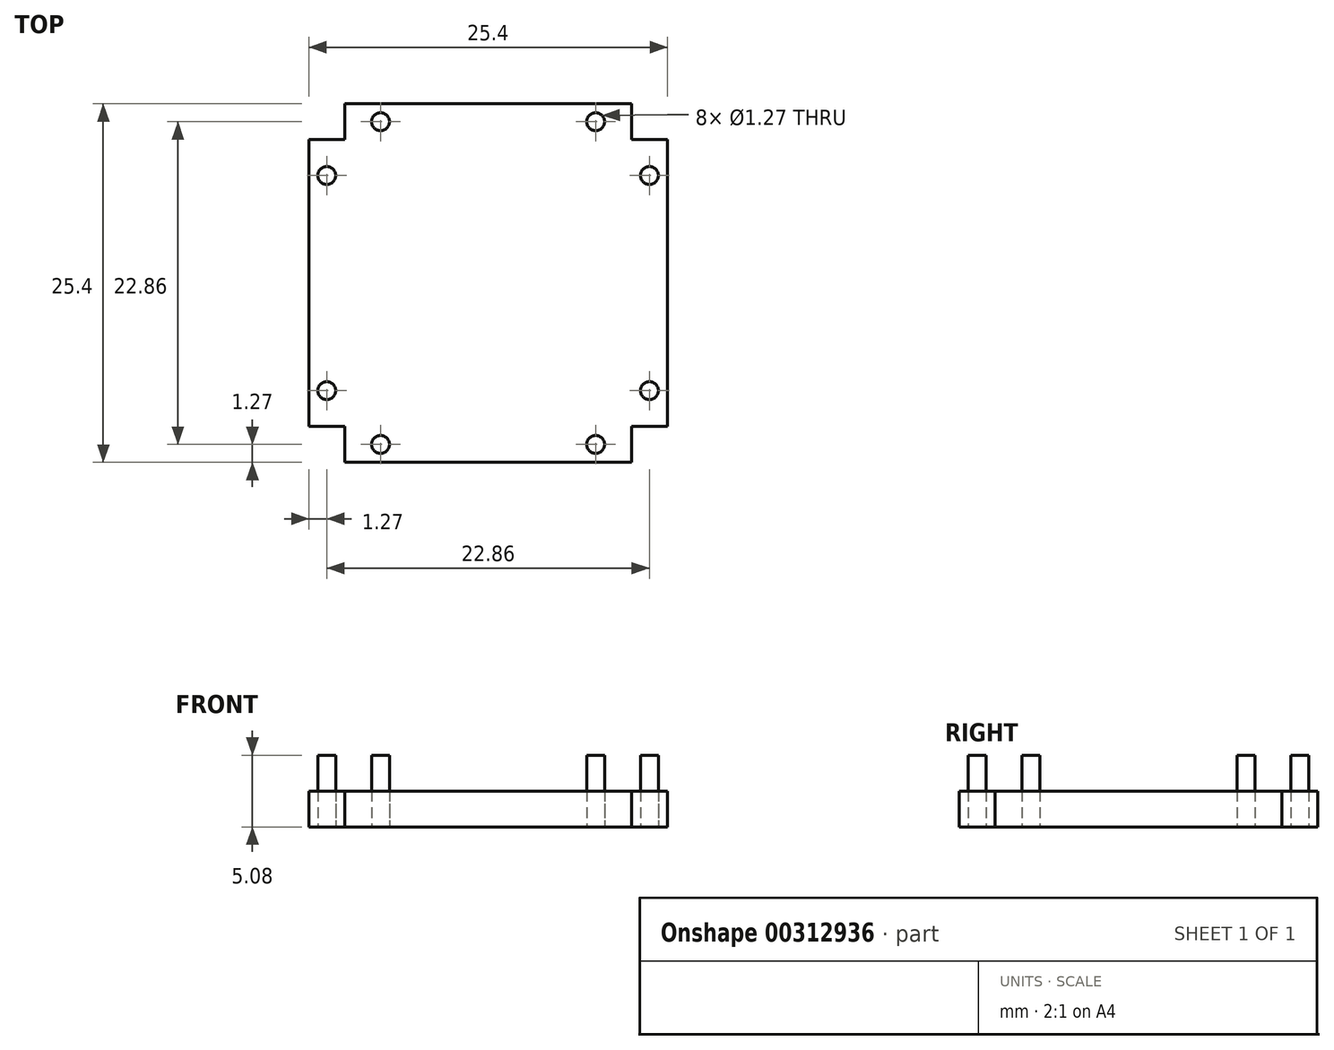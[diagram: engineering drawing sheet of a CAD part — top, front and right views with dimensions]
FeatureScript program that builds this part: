
annotation { "Feature Type Name" : "Feature", "Feature Type Description" : "" }
export const myFeature = defineFeature(function(context is Context, id is Id, definition is map)
    precondition{}
    {
        {
            var Q0;
            Q0=qCreatedBy(makeId("Top.planeOp"),FACE);
            var sketch = newSketch(context, id + "F0", { "sketchPlane" : qUnion([Q0])});
            skPoint(sketch, "E0.middle", {"position": v(0, 0) * mm});
            skLineSegment(sketch, "E1.bottom", {"start": v(10.16, -10.16) * mm, "end": v(-10.16, -10.16) * mm});
            skLineSegment(sketch, "E1.top", {"start": v(10.16, 10.16) * mm, "end": v(-10.16, 10.16) * mm});
            skLineSegment(sketch, "E1.left", {"start": v(10.16, -10.16) * mm, "end": v(10.16, 10.16) * mm});
            skLineSegment(sketch, "E1.right", {"start": v(-10.16, -10.16) * mm, "end": v(-10.16, 10.16) * mm});
            skLineSegment(sketch, "E2.bottom", {"start": v(-10.16, 10.16) * mm, "end": v(-12.7, 10.16) * mm});
            skLineSegment(sketch, "E2.left", {"start": v(-10.16, 10.16) * mm, "end": v(-10.16, 12.7) * mm});
            skLineSegment(sketch, "E3.bottom", {"start": v(10.16, 10.16) * mm, "end": v(12.7, 10.16) * mm});
            skLineSegment(sketch, "E3.left", {"start": v(10.16, 10.16) * mm, "end": v(10.16, 12.7) * mm});
            skLineSegment(sketch, "E4.bottom", {"start": v(10.16, -10.16) * mm, "end": v(12.7, -10.16) * mm});
            skLineSegment(sketch, "E4.left", {"start": v(10.16, -10.16) * mm, "end": v(10.16, -12.7) * mm});
            skLineSegment(sketch, "E5.bottom", {"start": v(-10.16, -10.16) * mm, "end": v(-12.7, -10.16) * mm});
            skLineSegment(sketch, "E5.left", {"start": v(-10.16, -10.16) * mm, "end": v(-10.16, -12.7) * mm});
            skLineSegment(sketch, "E6", {"start": v(-10.16, 12.7) * mm, "end": v(10.16, 12.7) * mm});
            skLineSegment(sketch, "E7", {"start": v(-12.7, 10.16) * mm, "end": v(-12.7, -10.16) * mm});
            skLineSegment(sketch, "E8", {"start": v(-10.16, -12.7) * mm, "end": v(10.16, -12.7) * mm});
            skLineSegment(sketch, "E9", {"start": v(12.7, 10.16) * mm, "end": v(12.7, -10.16) * mm});
            skCircle(sketch, "E10", {"center": v(-7.62, 11.43) * mm, "radius": 0.64 * mm});
            skCircle(sketch, "E11", {"center": v(7.62, 11.43) * mm, "radius": 0.64 * mm});
            skCircle(sketch, "E12", {"center": v(11.43, 7.62) * mm, "radius": 0.64 * mm});
            skCircle(sketch, "E13", {"center": v(-11.43, 7.62) * mm, "radius": 0.64 * mm});
            skCircle(sketch, "E14", {"center": v(-11.43, -7.62) * mm, "radius": 0.64 * mm});
            skCircle(sketch, "E15", {"center": v(-7.62, -11.43) * mm, "radius": 0.64 * mm});
            skCircle(sketch, "E16", {"center": v(7.62, -11.43) * mm, "radius": 0.64 * mm});
            skCircle(sketch, "E17", {"center": v(11.43, -7.62) * mm, "radius": 0.64 * mm});
            skSolve(sketch);
        }
        {
            var Q0;
            Q0=makeQuery(id+"F0.imprint","IMPRINT",FACE,{"disambiguationData":[TD([[makeQuery(id+"F0.imprint","IMPRINT",EDGE,{"derivedFrom":sQuery(id+"F0.wireOp",EDGE,"E1.right")}),1.0]])]});
            var Q1;
            Q1=makeQuery(id+"F0.imprint","IMPRINT",FACE,{"disambiguationData":[TD([[makeQuery(id+"F0.imprint","IMPRINT",EDGE,{"derivedFrom":sQuery(id+"F0.wireOp",EDGE,"E1.top")}),-1.0]])]});
            var Q2;
            Q2=makeQuery(id+"F0.imprint","IMPRINT",FACE,{"disambiguationData":[TD([[makeQuery(id+"F0.imprint","IMPRINT",EDGE,{"derivedFrom":sQuery(id+"F0.wireOp",EDGE,"E1.bottom")}),-1.0]])]});
            var Q3;
            Q3=makeQuery(id+"F0.imprint","IMPRINT",FACE,{"disambiguationData":[TD([[makeQuery(id+"F0.imprint","IMPRINT",EDGE,{"derivedFrom":sQuery(id+"F0.wireOp",EDGE,"E1.bottom")}),1.0]])]});
            var Q4;
            Q4=makeQuery(id+"F0.imprint","IMPRINT",FACE,{"disambiguationData":[TD([[makeQuery(id+"F0.imprint","IMPRINT",EDGE,{"derivedFrom":sQuery(id+"F0.wireOp",EDGE,"E1.left")}),-1.0]])]});
            extrude(context, id + "F1", {"entities" : qUnion([Q0, Q1, Q2, Q3, Q4]), "depth" : 2.54 * mm});
        }
        {
            var Q0;
            Q0=makeQuery(id+"F0.imprint","IMPRINT",FACE,{"disambiguationData":[TD([[makeQuery(id+"F0.imprint","IMPRINT",EDGE,{"derivedFrom":sQuery(id+"F0.wireOp",EDGE,"E13")}),1.0]])]});
            var Q1;
            Q1=makeQuery(id+"F0.imprint","IMPRINT",FACE,{"disambiguationData":[TD([[makeQuery(id+"F0.imprint","IMPRINT",EDGE,{"derivedFrom":sQuery(id+"F0.wireOp",EDGE,"E10")}),1.0]])]});
            var Q2;
            Q2=makeQuery(id+"F0.imprint","IMPRINT",FACE,{"disambiguationData":[TD([[makeQuery(id+"F0.imprint","IMPRINT",EDGE,{"derivedFrom":sQuery(id+"F0.wireOp",EDGE,"E11")}),1.0]])]});
            var Q3;
            Q3=makeQuery(id+"F0.imprint","IMPRINT",FACE,{"disambiguationData":[TD([[makeQuery(id+"F0.imprint","IMPRINT",EDGE,{"derivedFrom":sQuery(id+"F0.wireOp",EDGE,"E12")}),1.0]])]});
            var Q4;
            Q4=makeQuery(id+"F0.imprint","IMPRINT",FACE,{"disambiguationData":[TD([[makeQuery(id+"F0.imprint","IMPRINT",EDGE,{"derivedFrom":sQuery(id+"F0.wireOp",EDGE,"E17")}),1.0]])]});
            var Q5;
            Q5=makeQuery(id+"F0.imprint","IMPRINT",FACE,{"disambiguationData":[TD([[makeQuery(id+"F0.imprint","IMPRINT",EDGE,{"derivedFrom":sQuery(id+"F0.wireOp",EDGE,"E16")}),1.0]])]});
            var Q6;
            Q6=makeQuery(id+"F0.imprint","IMPRINT",FACE,{"disambiguationData":[TD([[makeQuery(id+"F0.imprint","IMPRINT",EDGE,{"derivedFrom":sQuery(id+"F0.wireOp",EDGE,"E15")}),1.0]])]});
            var Q7;
            Q7=makeQuery(id+"F0.imprint","IMPRINT",FACE,{"disambiguationData":[TD([[makeQuery(id+"F0.imprint","IMPRINT",EDGE,{"derivedFrom":sQuery(id+"F0.wireOp",EDGE,"E14")}),1.0]])]});
            extrude(context, id + "F2", {"entities" : qUnion([Q0, Q1, Q2, Q3, Q4, Q5, Q6, Q7]), "depth" : 5.08 * mm});
        }
    });
